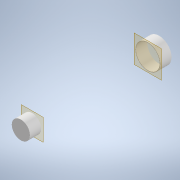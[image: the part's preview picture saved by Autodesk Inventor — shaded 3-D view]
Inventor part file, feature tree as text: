
AUTODESK INVENTOR PART (.ipt)
format: ipt  version: 2020 (Build 240168000, 168)  size: 110,080 bytes
history: native  units: mm
features: plane x2, extrude x2, sketch x2, other x2
ambient origin geometry x8: Origin, YZ Plane, XZ Plane, XY Plane, X Axis, Y Axis, Z Axis, Center Point
bodies: Solid1 (feature_tree)
feature tree (8):
  plane  "Work Plane1"
  plane  "Work Plane2"
  extrude  "Extrusion1"  Depth=20.0mm TaperAngle=0.0deg
  extrude  "Extrusion2"  Depth=33.0mm
  sketch  "Sketch1"  dims[d1=20.0mm d2=0.0mm d4=20.0mm d5=0.0mm]
  sketch  "Sketch2"  dims[d6=45.5mm d7=33.0mm]
  other  "Assembly1"
  other  "oar:1"
